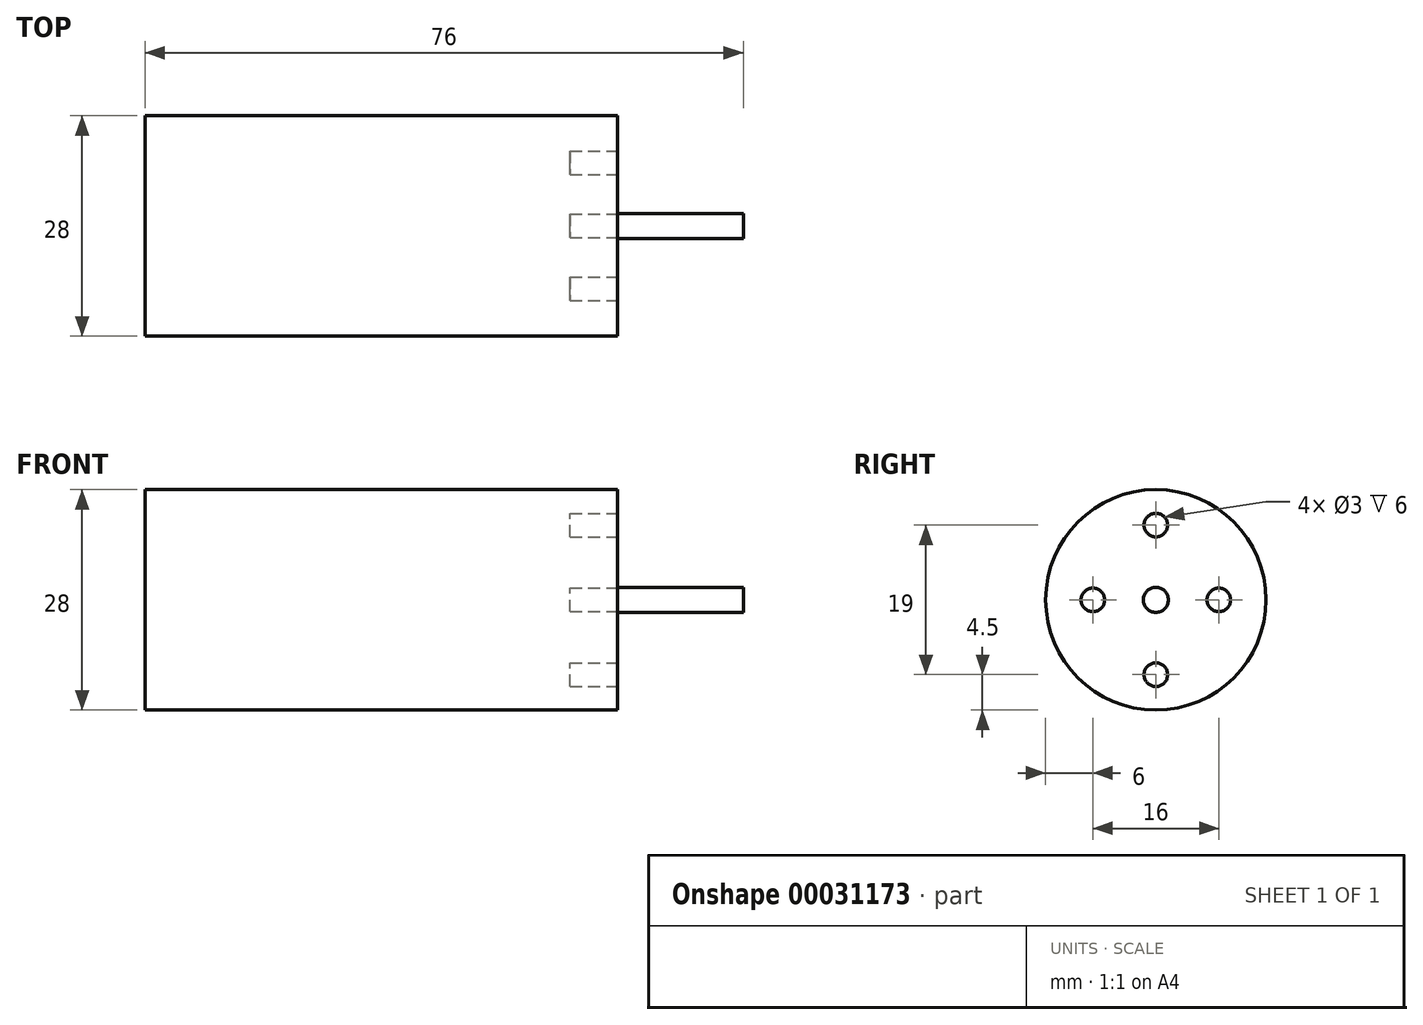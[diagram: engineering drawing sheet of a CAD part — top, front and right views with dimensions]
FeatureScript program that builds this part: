
annotation { "Feature Type Name" : "Feature", "Feature Type Description" : "" }
export const myFeature = defineFeature(function(context is Context, id is Id, definition is map)
    precondition{}
    {
        {
            var Q0;
            Q0=qCreatedBy(makeId("Right.planeOp"),FACE);
            var sketch = newSketch(context, id + "F0", { "sketchPlane" : qUnion([Q0])});
            skCircle(sketch, "E0", {"center": v(0, 0) * mm, "radius": 14 * mm});
            skSolve(sketch);
        }
        {
            var Q0;
            Q0 = qSketchRegion(id + "F0", true);
            extrude(context, id + "F1", {"entities" : qUnion([Q0]), "oppositeDirection" : true, "depth" : 60 * mm});
        }
        {
            var Q0;
            Q0=makeQuery(id+"F1.opExtrude","CAP_FACE",FACE,{"disambiguationData":[OSD([sQuery(id+"F0.wireOp",EDGE,"E0")])],"isStart":true});
            var sketch = newSketch(context, id + "F2", { "sketchPlane" : qUnion([Q0])});
            skCircle(sketch, "E1", {"center": v(0, 0) * mm, "radius": 1.59 * mm});
            skSolve(sketch);
        }
        {
            var Q0;
            Q0 = qSketchRegion(id + "F2", true);
            extrude(context, id + "F3", {"entities" : qUnion([Q0]), "operationType" : NewBodyOperationType.ADD, "depth" : 16 * mm});
        }
        {
            var Q0;
            Q0=makeQuery(id+"F1.opExtrude","CAP_FACE",FACE,{"disambiguationData":[OSD([sQuery(id+"F0.wireOp",EDGE,"E0")])],"isStart":true});
            var sketch = newSketch(context, id + "F4", { "sketchPlane" : qUnion([Q0])});
            skCircle(sketch, "E2", {"center": v(0, 0) * mm, "radius": 8 * mm, "construction": true});
            skCircle(sketch, "E3", {"center": v(0, 0) * mm, "radius": 9.5 * mm, "construction": true});
            skCircle(sketch, "E4", {"center": v(0, 9.5) * mm, "radius": 1.5 * mm});
            skCircle(sketch, "E5", {"center": v(8, 0) * mm, "radius": 1.5 * mm});
            skCircle(sketch, "E6", {"center": v(0, -9.5) * mm, "radius": 1.5 * mm});
            skCircle(sketch, "E7", {"center": v(-8, 0) * mm, "radius": 1.5 * mm});
            skSolve(sketch);
        }
        {
            var Q0;
            Q0 = qSketchRegion(id + "F4", true);
            extrude(context, id + "F5", {"entities" : qUnion([Q0]), "operationType" : NewBodyOperationType.REMOVE, "oppositeDirection" : true, "depth" : 6 * mm});
        }
    });
